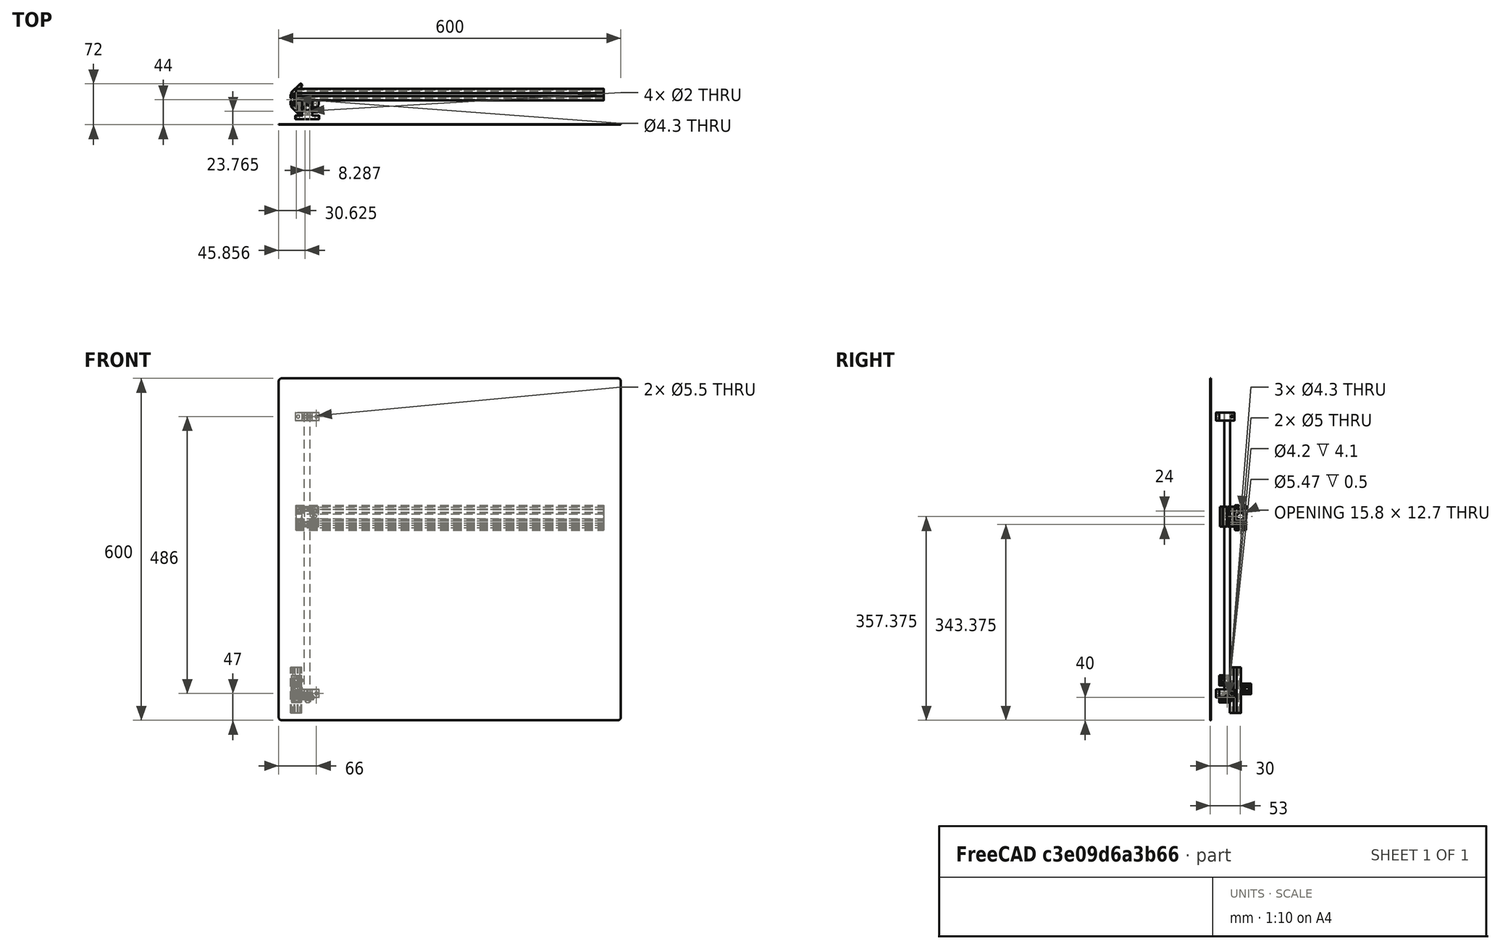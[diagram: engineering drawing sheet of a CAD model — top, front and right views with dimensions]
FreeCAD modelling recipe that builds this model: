
FCSTD DOCUMENT  (FreeCAD 0.19R)
Label: Assembler2
License: All rights reserved
LicenseURL: http://en.wikipedia.org/wiki/All_rights_reserved
objects: Part::Feature×18, App::Part×6, Part::FeaturePython×6, Part::Cylinder×5, Part::Box×1, Part::Fillet×1
note: 31 computed .brp shape members not serialized (recipe doc carries the construction recipe); baked Part::Feature solids carry a one-line shape summary decoded from their .brp

FEATURE [Part::Cylinder] Cylinder
  Angle = 360
  AttacherType = Attacher::AttachEngine3D
  Height = 500
  Radius = 5
FEATURE [Part::Feature] Feature  label="Motedis_SH012"
  Placement = pos=(0,-20,0) rot=(0,0,1;0rad)
  shape: bbox 42.01 x 32.81 x 14.01 mm, 71 faces, 2 solids (baked)
FEATURE [Part::Feature] Feature001  label="Motedis_SH013"
  Placement = pos=(0,-20,486) rot=(0,0,1;0rad)
  shape: bbox 42.01 x 32.81 x 14.01 mm, 71 faces, 2 solids (baked)
FEATURE [Part::Cylinder] Cylinder001
  Angle = 360
  AttacherType = Attacher::AttachEngine3D
  Height = 500
  Radius = 5
FEATURE [Part::Feature] Feature002  label="Motedis_SH014"
  Placement = pos=(0,-20,0) rot=(0,0,1;0rad)
  shape: bbox 42.01 x 32.81 x 14.01 mm, 71 faces, 2 solids (baked)
FEATURE [Part::Feature] Feature003  label="Motedis_SH015"
  Placement = pos=(0,-20,486) rot=(0,0,1;0rad)
  shape: bbox 42.01 x 32.81 x 14.01 mm, 71 faces, 2 solids (baked)
FEATURE [Part::Box] Box  label="Cube"
  AttacherType = Attacher::AttachEngine3D
  Height = 600
  Length = 600
  Placement = pos=(-50,-30,-40) rot=(0,0,1;0rad)
  Width = 1
FEATURE [Part::Fillet] Fillet
  Base = -> Box
  Edges = 4 edges r=5: [Edge2,Edge4,Edge6,Edge8]
FEATURE [Part::Feature] Feature004  label="SC10AJUU001"
  Placement = pos=(0,0,300) rot=(0,0,1;0rad)
  shape: bbox 40.02 x 26.02 x 35.02 mm, 83 faces, 4 solids (baked)
FEATURE [App::Part] Part  label="Welle1"
  Group = -> [Cylinder,Feature,Feature001,Feature004]
  Origin = -> Origin
FEATURE [Part::Feature] Feature005  label="SC10AJUU002"
  Placement = pos=(0,0,300) rot=(0,0,1;0rad)
  shape: bbox 40.02 x 26.02 x 35.02 mm, 83 faces, 4 solids (baked)
FEATURE [App::Part] Part001  label="Welle002"
  Group = -> [Cylinder001,Feature002,Feature003,Feature005]
  Origin = -> Origin001
  Placement = pos=(500,0,0) rot=(0,0,1;0rad)
FEATURE [Part::Feature] Extrude001001  label="540Profile_40x40slot5"
  Placement = pos=(-520,33,300) rot=(0,1,0;1.5708rad)
  shape: bbox 540 x 20 x 20 mm, 75 faces (baked)
FEATURE [Part::Feature] Cut001003  label="Tire001"
  Placement = pos=(1,0,0) rot=(0,0,1;0rad)
  shape: bbox 8.8 x 18.03 x 18.03 mm, 6 faces (baked)
FEATURE [Part::Feature] Cut001005  label="Tire002"
  Placement = pos=(1,0,0) rot=(0,0,1;0rad)
  shape: bbox 8.8 x 18.03 x 18.03 mm, 6 faces (baked)
FEATURE [Part::FeaturePython] Nut001  label="M5-Nut001"  # Fasteners workbench fastener (typed FeaturePython)
  Placement = pos=(11,0,0) rot=(0,-1,0;1.5708rad)
  diameter = 3
  invert = false
  matchOuter = false
  offset = 0
  thread = false
  type = 5
FEATURE [Part::FeaturePython] Nut002  label="M5-Nut002"  # Fasteners workbench fastener (typed FeaturePython)
  Placement = pos=(11,0,0) rot=(0,-1,0;1.5708rad)
  diameter = 3
  invert = false
  matchOuter = false
  offset = 0
  thread = false
  type = 5
FEATURE [Part::FeaturePython] Nut003  label="M5-Nut003"  # Fasteners workbench fastener (typed FeaturePython)
  Placement = pos=(11,0,0) rot=(0,-1,0;1.5708rad)
  diameter = 3
  invert = false
  matchOuter = false
  offset = 0
  thread = false
  type = 5
FEATURE [Part::Feature] Solid002  label="M5WinkelProfile20x20_2"
  Placement = pos=(-10,4,30) rot=(0,0,1;1.5708rad)
  shape: bbox 19.8 x 19.8 x 18 mm, 176 faces (baked)
FEATURE [Part::Feature] Extrude001002  label="15cmProfile_15x15"
  Placement = pos=(-16,24,-527) rot=(0,0,1;0rad)
  shape: bbox 20 x 20 x 80 mm, 75 faces (baked)
FEATURE [Part::FeaturePython] Screw002  label="M5x25-Screw001"  # Fasteners workbench fastener (typed FeaturePython)
  Placement = pos=(-13,0,0) rot=(0,-1,0;1.5708rad)
  diameter = 3
  invert = false
  length = 5
  lengthCustom = 25
  matchOuter = false
  offset = 1
  thread = false
  type = 12
FEATURE [Part::Cylinder] Cylinder005  label="Spacer001"
  Angle = 360
  AttacherType = Attacher::AttachEngine3D
  Height = 6
  Placement = pos=(-10,0,0) rot=(0,1,0;1.5708rad)
  Radius = 3.5
FEATURE [Part::Feature] Cut001006  label="Bearing001"
  Placement = pos=(1,0,0) rot=(0,0,1;0rad)
  shape: bbox 10 x 10 x 10 mm, 4 faces (baked)
FEATURE [Part::Feature] Cut001002  label="Bearing002"
  Placement = pos=(1,0,0) rot=(0,0,1;0rad)
  shape: bbox 10 x 10 x 10 mm, 4 faces (baked)
FEATURE [Part::Cylinder] Cylinder006  label="Spacer002"
  Angle = 360
  AttacherType = Attacher::AttachEngine3D
  Height = 6
  Placement = pos=(-10,0,0) rot=(0,1,0;1.5708rad)
  Radius = 3.5
FEATURE [Part::FeaturePython] Screw003  label="M5x25-Screw004"  # Fasteners workbench fastener (typed FeaturePython)
  Placement = pos=(-13,0,0) rot=(0,-1,0;1.5708rad)
  diameter = 3
  invert = false
  length = 5
  lengthCustom = 25
  matchOuter = false
  offset = 1
  thread = false
  type = 12
FEATURE [Part::Feature] Cut001007  label="Tire003"
  Placement = pos=(1,0,0) rot=(0,0,1;0rad)
  shape: bbox 8.8 x 18.03 x 18.03 mm, 6 faces (baked)
FEATURE [Part::Cylinder] Cylinder007  label="Spacer003"
  Angle = 360
  AttacherType = Attacher::AttachEngine3D
  Height = 6
  Placement = pos=(-10,0,0) rot=(0,1,0;1.5708rad)
  Radius = 3.5
FEATURE [App::Part] Part005  label="Rollensatz_Aliexpress4000394459606"
  Group = -> [Screw002,Cut001007,Cut001006,Cylinder007,Nut003]
  Origin = -> Origin005
  Placement = pos=(0,-4,0) rot=(0,0,1;0rad)
FEATURE [Part::Feature] Cut001004  label="Bearing003"
  Placement = pos=(1,0,0) rot=(0,0,1;0rad)
  shape: bbox 10 x 10 x 10 mm, 4 faces (baked)
FEATURE [Part::Feature] Solid003  label="M5WinkelProfile20x20_3"
  Placement = pos=(-10,24,15) rot=(0.707107,-0.707107,0;3.14159rad)
  shape: bbox 19.8 x 19.8 x 18 mm, 176 faces (baked)
FEATURE [Part::FeaturePython] Screw004  label="M5x25-Screw003"  # Fasteners workbench fastener (typed FeaturePython)
  Placement = pos=(-13,0,0) rot=(0,-1,0;1.5708rad)
  diameter = 3
  invert = false
  length = 5
  lengthCustom = 25
  matchOuter = false
  offset = 1
  thread = false
  type = 12
FEATURE [App::Part] Part003  label="Rollensatz_Aliexpress4000394459605_2"
  Group = -> [Screw004,Cut001003,Cut001002,Cylinder005,Nut001]
  Origin = -> Origin004
  Placement = pos=(0,-4,30) rot=(0,0,1;0rad)
FEATURE [Part::Feature] Solid001  label="M5WinkelProfile20x20"
  Placement = pos=(-10,4,0) rot=(0,0,1;1.5708rad)
  shape: bbox 19.8 x 19.8 x 18 mm, 176 faces (baked)
FEATURE [App::Part] Part006  label="Rollensatz_Aliexpress4000394459605_3"
  Group = -> [Screw003,Cut001005,Cut001004,Cylinder006,Nut002]
  Origin = -> Origin003
  Placement = pos=(0,33,15) rot=(0,0,1;0rad)
FEATURE [App::Part] Part004  label="Cart"
  Group = -> [Part005,Part003,Part006,Extrude001002,Solid001,Solid002,Solid003]
  Origin = -> Origin006
  Placement = pos=(250,8,300) rot=(0,-1,0;1.5708rad)
FEATURE [Part::Feature] Extrude001004001
  Placement = pos=(-21,33,324) rot=(0,1,0;1.5708rad)
  shape: bbox 540 x 20 x 40 mm, 120 faces (baked)
